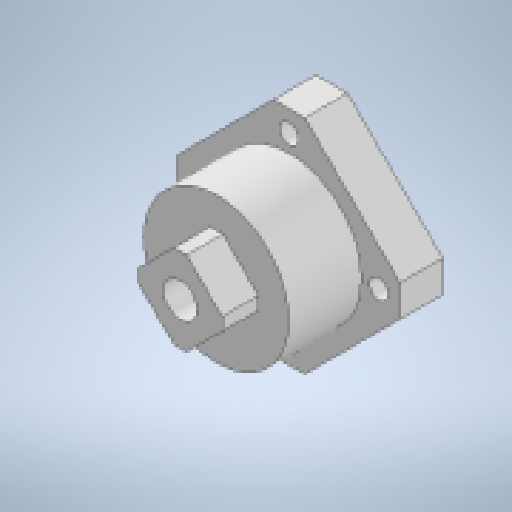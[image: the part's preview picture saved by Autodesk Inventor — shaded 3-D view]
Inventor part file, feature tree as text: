
AUTODESK INVENTOR PART (.ipt)
format: ipt  version: 2023 (Build 270158000, 158)  size: 301,568 bytes
history: native  units: mm
features: extrude x4, sketch x4
ambient origin geometry x8: Origin, YZ Plane, XZ Plane, XY Plane, X Axis, Y Axis, Z Axis, Center Point
bodies: Solid1 (feature_tree)
feature tree (8):
  extrude  "Extrusion1"  Depth=42.0mm
  extrude  "Extrusion2"  Depth=42.0mm
  extrude  "Extrusion3"  Depth=52.0mm
  extrude  "Extrusion4"  Depth=8.5mm
  sketch  "Sketch1"  dims[d0=10.0mm d1=42.0mm]
  sketch  "Sketch2"  dims[d2=135.0deg d3=42.0mm]
  sketch  "Sketch3"  dims[d4=4.5mm d5=52.0mm]
  sketch  "Sketch5"  dims[d6=10.0mm d7=0.0mm d8=34.0mm d9=17.0mm d10=0.0mm d11=8.0mm d12=4.0mm d13=0.0mm d14=16.0mm d15=3.0mm d16=10.0mm d17=8.5mm d18=0.0mm]
